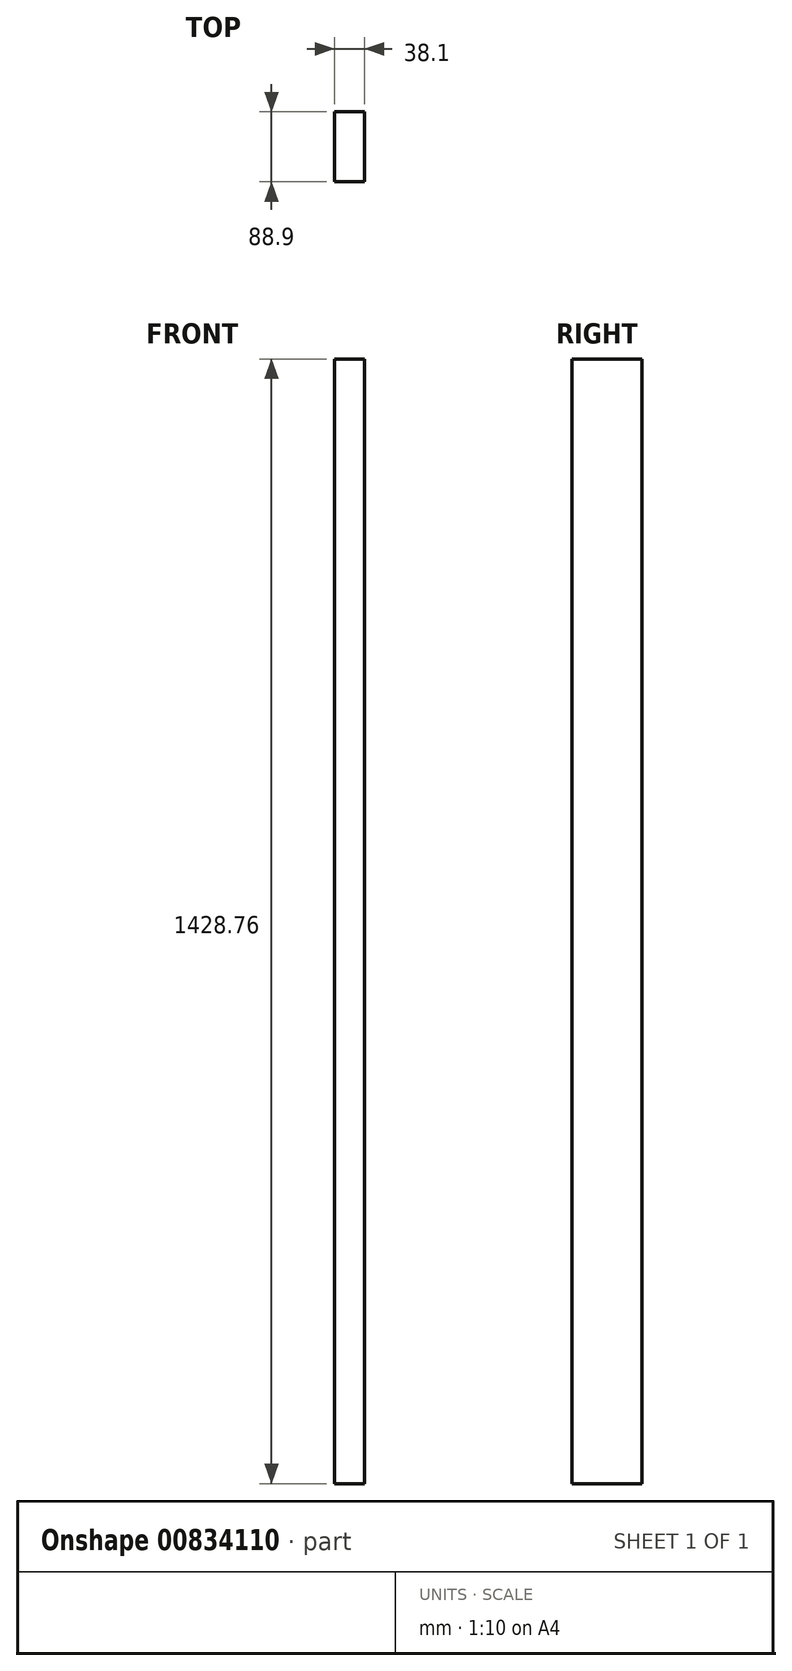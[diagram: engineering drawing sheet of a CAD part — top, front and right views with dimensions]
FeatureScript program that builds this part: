
annotation { "Feature Type Name" : "Feature", "Feature Type Description" : "" }
export const myFeature = defineFeature(function(context is Context, id is Id, definition is map)
    precondition{}
    {
        {
            var Q0;
            Q0=qCreatedBy(makeId("Top.planeOp"),FACE);
            var sketch = newSketch(context, id + "F0", { "sketchPlane" : qUnion([Q0])});
            skLineSegment(sketch, "E0.bottom", {"start": v(19.05, -44.45) * mm, "end": v(-19.05, -44.45) * mm});
            skLineSegment(sketch, "E0.top", {"start": v(19.05, 44.45) * mm, "end": v(-19.05, 44.45) * mm});
            skLineSegment(sketch, "E0.left", {"start": v(19.05, -44.45) * mm, "end": v(19.05, 44.45) * mm});
            skLineSegment(sketch, "E0.right", {"start": v(-19.05, -44.45) * mm, "end": v(-19.05, 44.45) * mm});
            skPoint(sketch, "E0.middle", {"position": v(0, 0) * mm});
            skSolve(sketch);
        }
        {
            var Q0;
            Q0=qSketchRegion(id+"F0",true);
            extrude(context, id + "F1", {"entities" : qUnion([Q0]), "endBound" : BoundingType.SYMMETRIC, "depth" : 1428.75 * mm});
        }
    });
